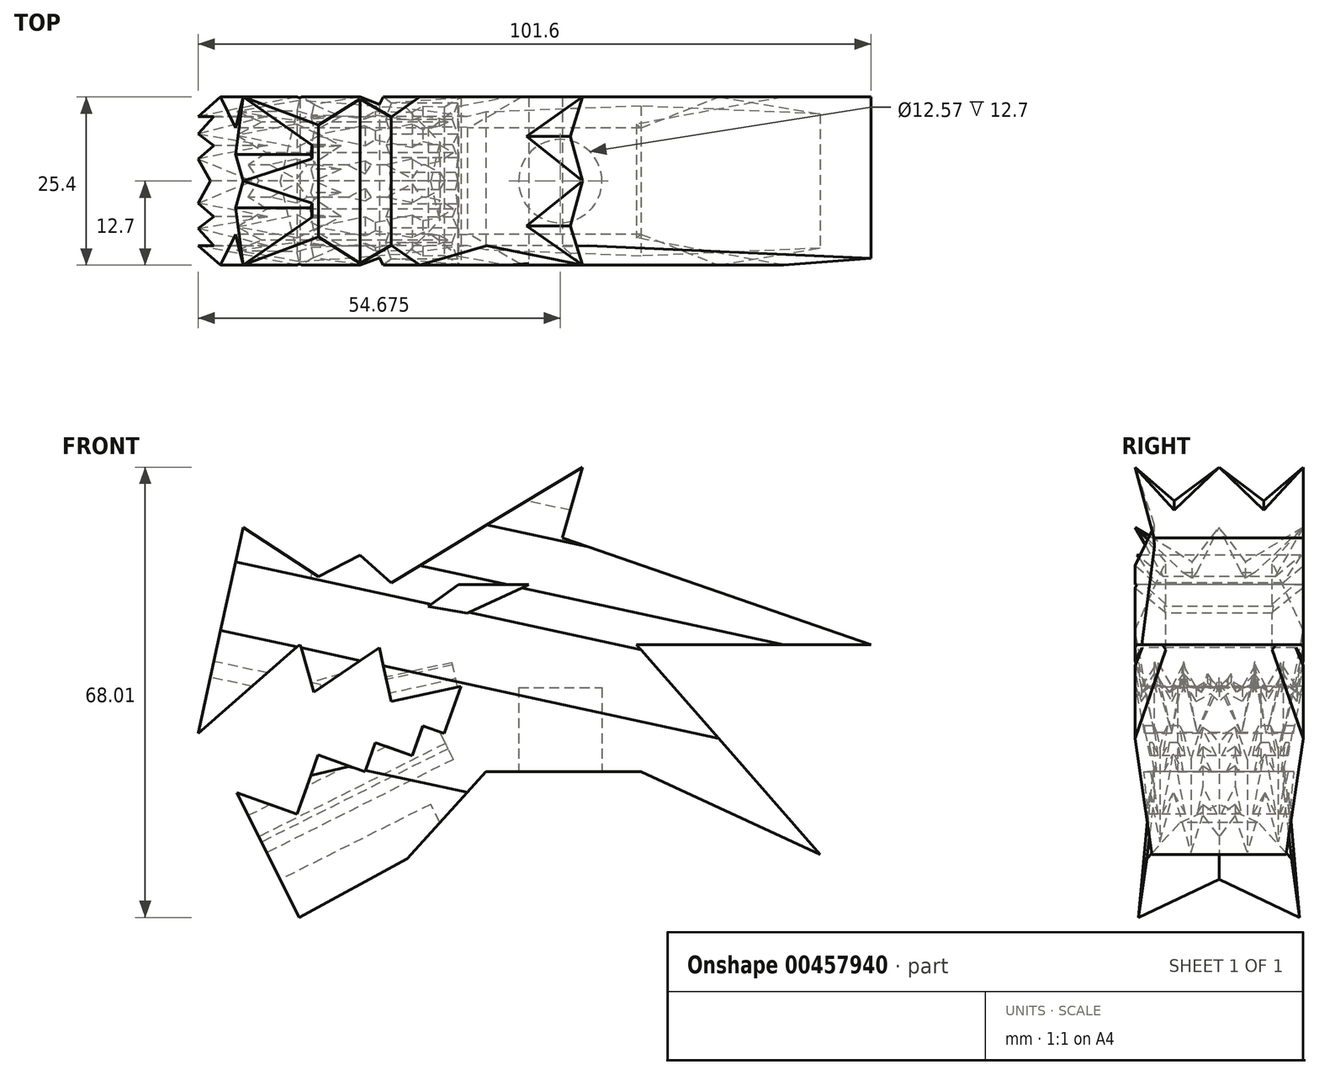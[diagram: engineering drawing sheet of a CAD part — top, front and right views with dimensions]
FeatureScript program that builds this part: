
annotation { "Feature Type Name" : "Feature", "Feature Type Description" : "" }
export const myFeature = defineFeature(function(context is Context, id is Id, definition is map)
    precondition{}
    {
        {
            var Q0;
            Q0=qCreatedBy(makeId("Front.planeOp"),FACE);
            var sketch = newSketch(context, id + "F0", { "sketchPlane" : qUnion([Q0])});
            skLineSegment(sketch, "E0", {"start": v(0, 0) * mm, "end": v(-25.28, -27.85) * mm});
            skLineSegment(sketch, "E1", {"start": v(-25.28, -27.85) * mm, "end": v(-37.63, -3.15) * mm});
            skLineSegment(sketch, "E2", {"start": v(-37.63, -3.15) * mm, "end": v(-28.55, -6.4) * mm});
            skLineSegment(sketch, "E3", {"start": v(-28.55, -6.4) * mm, "end": v(-25.34, 2.53) * mm});
            skLineSegment(sketch, "E4", {"start": v(-25.34, 2.53) * mm, "end": v(-18.28, 0) * mm});
            skLineSegment(sketch, "E5", {"start": v(-18.28, 0) * mm, "end": v(-16.7, 4.4) * mm});
            skLineSegment(sketch, "E6", {"start": v(-16.7, 4.4) * mm, "end": v(-11.16, 2.42) * mm});
            skLineSegment(sketch, "E7", {"start": v(-11.16, 2.42) * mm, "end": v(-9.54, 6.93) * mm});
            skLineSegment(sketch, "E8", {"start": v(-9.54, 6.93) * mm, "end": v(-6.35, 5.78) * mm});
            skLineSegment(sketch, "E9", {"start": v(-6.35, 5.78) * mm, "end": v(-3.79, 12.91) * mm});
            skLineSegment(sketch, "E10", {"start": v(-3.79, 12.91) * mm, "end": v(-14.33, 10.6) * mm});
            skLineSegment(sketch, "E11", {"start": v(-14.33, 10.6) * mm, "end": v(-16.11, 18.75) * mm});
            skLineSegment(sketch, "E12", {"start": v(-16.11, 18.75) * mm, "end": v(-25.98, 12) * mm});
            skLineSegment(sketch, "E13", {"start": v(-25.98, 12) * mm, "end": v(-28.08, 19.22) * mm});
            skLineSegment(sketch, "E14", {"start": v(-28.08, 19.22) * mm, "end": v(-43.46, 5.78) * mm});
            skLineSegment(sketch, "E15", {"start": v(-43.46, 5.78) * mm, "end": v(-36.7, 36.93) * mm});
            skLineSegment(sketch, "E16", {"start": v(-36.7, 36.93) * mm, "end": v(-25.28, 29.48) * mm});
            skLineSegment(sketch, "E17", {"start": v(-25.28, 29.48) * mm, "end": v(-19, 32.74) * mm});
            skLineSegment(sketch, "E18", {"start": v(-19, 32.74) * mm, "end": v(-14.33, 28.55) * mm});
            skLineSegment(sketch, "E19", {"start": v(-14.33, 28.55) * mm, "end": v(14.56, 46.02) * mm});
            skLineSegment(sketch, "E20", {"start": v(14.56, 46.02) * mm, "end": v(11.53, 35.3) * mm});
            skLineSegment(sketch, "E21", {"start": v(11.53, 35.3) * mm, "end": v(58.14, 19.22) * mm});
            skLineSegment(sketch, "E22", {"start": v(58.14, 19.22) * mm, "end": v(22.72, 19.22) * mm});
            skLineSegment(sketch, "E23", {"start": v(22.72, 19.22) * mm, "end": v(50.45, -12.47) * mm});
            skLineSegment(sketch, "E24", {"start": v(50.45, -12.47) * mm, "end": v(23.42, 0) * mm});
            skLineSegment(sketch, "E25", {"start": v(23.42, 0) * mm, "end": v(0, 0) * mm});
            skLineSegment(sketch, "E26", {"start": v(-8.76, 24.95) * mm, "end": v(-4.13, 28.26) * mm});
            skLineSegment(sketch, "E27", {"start": v(-4.13, 28.26) * mm, "end": v(6.44, 28.26) * mm});
            skLineSegment(sketch, "E28", {"start": v(6.44, 28.26) * mm, "end": v(-2.8, 23.96) * mm});
            skLineSegment(sketch, "E29", {"start": v(-2.8, 23.96) * mm, "end": v(-8.76, 24.95) * mm});
            skSolve(sketch);
        }
        {
            var Q0;
            Q0=makeQuery(id+"F0.imprint","IMPRINT",FACE,{"disambiguationData":[TD([[makeQuery(id+"F0.imprint","IMPRINT",EDGE,{"derivedFrom":sQuery(id+"F0.wireOp",EDGE,"E0")}),-1.0]])]});
            extrude(context, id + "F1", {"entities" : qUnion([Q0]), "oppositeDirection" : true, "depth" : 25.4 * mm, "offsetDistance" : 25.4 * mm});
        }
        {
            var Q0;
            Q0=makeQuery(id+"F1.opExtrude","SWEPT_FACE",FACE,{"disambiguationData":[OSD([sQuery(id+"F0.wireOp",EDGE,"E15")])]});
            cPlane(context, id + "F2", {"entities" : qUnion([Q0]), "cplaneType" : CPlaneType.OFFSET, "offset" : 25.4 * mm, "width" : 152.4 * mm, "height" : 152.4 * mm});
        }
        {
            var Q0;
            Q0=qCreatedBy(id+"F2.planeOp",FACE);
            var sketch = newSketch(context, id + "F3", { "sketchPlane" : qUnion([Q0])});
            skPoint(sketch, "E30.0", {"position": v(-25.4, 48.06) * mm});
            skPoint(sketch, "E31.0", {"position": v(0, 48.06) * mm});
            skPoint(sketch, "E32.0", {"position": v(-12.7, 48.06) * mm});
            skPoint(sketch, "E33.0", {"position": v(-12.7, 28.31) * mm});
            skPoint(sketch, "E34.0", {"position": v(-25.4, 28.31) * mm});
            skPoint(sketch, "E35.0", {"position": v(0, 28.31) * mm});
            skPoint(sketch, "E36.0", {"position": v(-25.4, 36.46) * mm});
            skPoint(sketch, "E37.0", {"position": v(0, 36.95) * mm});
            skPoint(sketch, "E38.0", {"position": v(-25.4, 12.38) * mm});
            skPoint(sketch, "E39.0", {"position": v(0, 12.38) * mm});
            skPoint(sketch, "E40.0", {"position": v(-25.4, 0) * mm});
            skPoint(sketch, "E41.0", {"position": v(0, 0) * mm});
            skPoint(sketch, "E42.0", {"position": v(-12.7, -3.56) * mm});
            skLineSegment(sketch, "E43", {"start": v(-25.4, 28.31) * mm, "end": v(-25.4, 48.06) * mm});
            skLineSegment(sketch, "E44", {"start": v(-12.7, 48.06) * mm, "end": v(-19.48, 41.3) * mm});
            skLineSegment(sketch, "E45", {"start": v(-19.48, 41.3) * mm, "end": v(-25.4, 48.06) * mm});
            skLineSegment(sketch, "E46", {"start": v(-25.4, 48.06) * mm, "end": v(-22.44, 36.46) * mm});
            skPoint(sketch, "E46.endSnap0", {"position": v(-22.44, 44.68) * mm});
            skLineSegment(sketch, "E47", {"start": v(-22.44, 36.46) * mm, "end": v(-25.4, 28.31) * mm});
            skLineSegment(sketch, "E48", {"start": v(-25.4, 28.31) * mm, "end": v(-20.73, 22.97) * mm});
            skLineSegment(sketch, "E49", {"start": v(-20.73, 22.97) * mm, "end": v(-25.4, 12.38) * mm});
            skLineSegment(sketch, "E50", {"start": v(-25.4, 12.38) * mm, "end": v(-22.44, -3.65) * mm});
            skLineSegment(sketch, "E51", {"start": v(-22.44, -3.65) * mm, "end": v(-25.4, -32.74) * mm});
            skLineSegment(sketch, "E52", {"start": v(-25.4, -32.74) * mm, "end": v(-12.7, -28.11) * mm});
            skLineSegment(sketch, "E53", {"start": v(-12.7, -28.11) * mm, "end": v(-12.7, -32.74) * mm});
            skLineSegment(sketch, "E54", {"start": v(-12.7, 48.06) * mm, "end": v(-12.7, -32.74) * mm});
            skLineSegment(sketch, "E55.MirrorCS", {"start": v(-12.7, 48.06) * mm, "end": v(-5.92, 41.3) * mm});
            skLineSegment(sketch, "E56.MirrorCS", {"start": v(-5.92, 41.3) * mm, "end": v(0, 48.06) * mm});
            skLineSegment(sketch, "E57.MirrorCS", {"start": v(0, 48.06) * mm, "end": v(-2.96, 36.46) * mm});
            skLineSegment(sketch, "E58.MirrorCS", {"start": v(-2.96, 36.46) * mm, "end": v(0, 28.31) * mm});
            skLineSegment(sketch, "E59.MirrorCS", {"start": v(0, 28.31) * mm, "end": v(-4.67, 22.97) * mm});
            skLineSegment(sketch, "E60.MirrorCS", {"start": v(-2.96, -3.65) * mm, "end": v(0, -32.74) * mm});
            skLineSegment(sketch, "E61.MirrorCS", {"start": v(0, 12.38) * mm, "end": v(-2.96, -3.65) * mm});
            skLineSegment(sketch, "E62.MirrorCS", {"start": v(-4.67, 22.97) * mm, "end": v(0, 12.38) * mm});
            skLineSegment(sketch, "E63.MirrorCS", {"start": v(0, -32.74) * mm, "end": v(-12.7, -28.11) * mm});
            skLineSegment(sketch, "E64", {"start": v(-35.26, 55.46) * mm, "end": v(-35.26, -53.24) * mm});
            skLineSegment(sketch, "E65", {"start": v(-35.26, -53.24) * mm, "end": v(17.4, -53.24) * mm});
            skLineSegment(sketch, "E66", {"start": v(17.4, -53.24) * mm, "end": v(14.5, 59.12) * mm});
            skLineSegment(sketch, "E67", {"start": v(14.5, 59.12) * mm, "end": v(-35.26, 55.46) * mm});
            skSolve(sketch);
        }
        {
            var Q0;
            Q0=makeQuery(id+"F3.imprint","IMPRINT",FACE,{"disambiguationData":[TD([[makeQuery(id+"F3.imprint","IMPRINT",EDGE,{"derivedFrom":sQuery(id+"F3.wireOp",EDGE,"E43")}),1.0]])]});
            extrude(context, id + "F4", {"entities" : qUnion([Q0]), "operationType" : NewBodyOperationType.REMOVE, "oppositeDirection" : true, "depth" : 169.93 * mm, "offsetDistance" : 25.4 * mm});
        }
        {
            var Q0;
            Q0=makeQuery(id+"F1.opExtrude","SWEPT_FACE",FACE,{"disambiguationData":[OSD([sQuery(id+"F0.wireOp",EDGE,"E15")])]});
            var sketch = newSketch(context, id + "F5", { "sketchPlane" : qUnion([Q0])});
            skPoint(sketch, "E68.0", {"position": v(-12.7, 28.31) * mm});
            skLineSegment(sketch, "E69", {"start": v(-12.7, 28.31) * mm, "end": v(-12.7, -3.56) * mm});
            skLineSegment(sketch, "E70", {"start": v(-25.4, 28.31) * mm, "end": v(-16.72, 22.98) * mm});
            skLineSegment(sketch, "E71", {"start": v(-16.72, 22.98) * mm, "end": v(-12.7, 28.31) * mm});
            skLineSegment(sketch, "E72.MirrorCS", {"start": v(-8.68, 22.98) * mm, "end": v(-12.7, 28.31) * mm});
            skLineSegment(sketch, "E73.MirrorCS", {"start": v(0, 28.31) * mm, "end": v(-8.68, 22.98) * mm});
            skLineSegment(sketch, "E74", {"start": v(-22.45, -3.56) * mm, "end": v(-22.45, 7.58) * mm});
            skLineSegment(sketch, "E75", {"start": v(-22.45, 7.58) * mm, "end": v(-19.84, -3.56) * mm});
            skLineSegment(sketch, "E76", {"start": v(-19.84, -3.56) * mm, "end": v(-18.06, 7.58) * mm});
            skLineSegment(sketch, "E77", {"start": v(-18.06, 7.58) * mm, "end": v(-16.05, -3.56) * mm});
            skLineSegment(sketch, "E78", {"start": v(-16.05, -3.56) * mm, "end": v(-12.7, 5.12) * mm});
            skLineSegment(sketch, "E79.MirrorCS", {"start": v(-9.35, -3.56) * mm, "end": v(-12.7, 5.12) * mm});
            skLineSegment(sketch, "E80.MirrorCS", {"start": v(-7.34, 7.58) * mm, "end": v(-9.35, -3.56) * mm});
            skLineSegment(sketch, "E81.MirrorCS", {"start": v(-5.56, -3.56) * mm, "end": v(-7.34, 7.58) * mm});
            skLineSegment(sketch, "E82.MirrorCS", {"start": v(-2.95, 7.58) * mm, "end": v(-5.56, -3.56) * mm});
            skLineSegment(sketch, "E83.MirrorCS", {"start": v(-2.95, -3.56) * mm, "end": v(-2.95, 7.58) * mm});
            skLineSegment(sketch, "E84", {"start": v(-22.45, -3.56) * mm, "end": v(-2.95, -3.56) * mm});
            skSolve(sketch);
        }
        {
            var Q0;
            {var subQ0=sQuery(id+"F5.wireOp",EDGE,"E70");Q0=makeQuery(id+"F5.imprint","IMPRINT",FACE,{"disambiguationData":[TD([[makeQuery(id+"F5.imprint","IMPRINT",EDGE,{"derivedFrom":subQ0}),1.0]])]});}
            var Q1;
            {var subQ0=sQuery(id+"F5.wireOp",EDGE,"E72.MirrorCS");Q1=makeQuery(id+"F5.imprint","IMPRINT",FACE,{"disambiguationData":[TD([[makeQuery(id+"F5.imprint","IMPRINT",EDGE,{"derivedFrom":subQ0}),-1.0]])]});}
            extrude(context, id + "F6", {"entities" : qUnion([Q0, Q1]), "operationType" : NewBodyOperationType.REMOVE, "oppositeDirection" : true, "depth" : 11.68 * mm, "offsetDistance" : 25.4 * mm});
        }
        {
            var Q0;
            Q0 = qSketchRegion(id + "F5", true);
            extrude(context, id + "F7", {"entities" : qUnion([Q0]), "operationType" : NewBodyOperationType.REMOVE, "oppositeDirection" : true, "depth" : 16.5 * mm, "offsetDistance" : 25.4 * mm});
        }
        {
            var Q0;
            Q0=makeQuery(id+"F1.opExtrude","SWEPT_FACE",FACE,{"disambiguationData":[OSD([sQuery(id+"F0.wireOp",EDGE,"E1")])]});
            var sketch = newSketch(context, id + "F8", { "sketchPlane" : qUnion([Q0])});
            skPoint(sketch, "E85.0", {"position": v(-12.7, 14.02) * mm});
            skPoint(sketch, "E86.0", {"position": v(-12.7, -7.87) * mm});
            skLineSegment(sketch, "E87", {"start": v(-12.7, 14.02) * mm, "end": v(-12.7, -7.87) * mm});
            skLineSegment(sketch, "E88", {"start": v(-23.2, 14.02) * mm, "end": v(-21.63, 5.68) * mm});
            skLineSegment(sketch, "E89", {"start": v(-21.63, 5.68) * mm, "end": v(-19.62, 14.02) * mm});
            skLineSegment(sketch, "E90", {"start": v(-19.62, 14.02) * mm, "end": v(-16.94, 3.9) * mm});
            skLineSegment(sketch, "E91", {"start": v(-16.94, 3.9) * mm, "end": v(-15.15, 10.14) * mm});
            skLineSegment(sketch, "E92", {"start": v(-15.15, 10.14) * mm, "end": v(-12.7, 6.57) * mm});
            skLineSegment(sketch, "E93.MirrorCS", {"start": v(-10.25, 10.14) * mm, "end": v(-12.7, 6.57) * mm});
            skLineSegment(sketch, "E94.MirrorCS", {"start": v(-8.46, 3.9) * mm, "end": v(-10.25, 10.14) * mm});
            skLineSegment(sketch, "E95.MirrorCS", {"start": v(-5.78, 14.02) * mm, "end": v(-8.46, 3.9) * mm});
            skLineSegment(sketch, "E96.MirrorCS", {"start": v(-3.77, 5.68) * mm, "end": v(-5.78, 14.02) * mm});
            skLineSegment(sketch, "E97.MirrorCS", {"start": v(-2.2, 14.02) * mm, "end": v(-3.77, 5.68) * mm});
            skSolve(sketch);
        }
        {
            var Q0;
            {var subQ1=sQuery(id+"F8.wireOp",EDGE,"E93.MirrorCS");Q0=makeQuery(id+"F8.imprint","IMPRINT",FACE,{"disambiguationData":[TD([[makeQuery(id+"F8.imprint","IMPRINT",EDGE,{"derivedFrom":subQ1}),-1.0]])]});}
            var Q1;
            {var subQ1=sQuery(id+"F8.wireOp",EDGE,"E90");Q1=makeQuery(id+"F8.imprint","IMPRINT",FACE,{"disambiguationData":[TD([[makeQuery(id+"F8.imprint","IMPRINT",EDGE,{"derivedFrom":subQ1}),1.0]])]});}
            var Q2;
            {var subQ0=sQuery(id+"F8.wireOp",EDGE,"E88");Q2=makeQuery(id+"F8.imprint","IMPRINT",FACE,{"disambiguationData":[TD([[makeQuery(id+"F8.imprint","IMPRINT",EDGE,{"derivedFrom":subQ0}),1.0]])]});}
            var Q3;
            {var subQ0=sQuery(id+"F8.wireOp",EDGE,"E96.MirrorCS");Q3=makeQuery(id+"F8.imprint","IMPRINT",FACE,{"disambiguationData":[TD([[makeQuery(id+"F8.imprint","IMPRINT",EDGE,{"derivedFrom":subQ0}),-1.0]])]});}
            extrude(context, id + "F9", {"entities" : qUnion([Q0, Q1, Q2, Q3]), "operationType" : NewBodyOperationType.REMOVE, "oppositeDirection" : true, "depth" : 31.5 * mm, "offsetDistance" : 25.4 * mm});
        }
        {
            var Q0;
            Q0=makeQuery(id+"F1.opExtrude","SWEPT_FACE",FACE,{"disambiguationData":[OSD([sQuery(id+"F0.wireOp",EDGE,"E11")])]});
            var sketch = newSketch(context, id + "F10", { "sketchPlane" : qUnion([Q0])});
            skPoint(sketch, "E98.0", {"position": v(-12.7, 17.28) * mm});
            skPoint(sketch, "E99.0", {"position": v(-12.7, 13.42) * mm});
            skLineSegment(sketch, "E100", {"start": v(-12.7, 13.42) * mm, "end": v(-12.7, 19.87) * mm});
            skLineSegment(sketch, "E101", {"start": v(-24.47, 13.42) * mm, "end": v(-21.99, 17.2) * mm});
            skLineSegment(sketch, "E102", {"start": v(-21.99, 17.2) * mm, "end": v(-19.8, 13.42) * mm});
            skLineSegment(sketch, "E103", {"start": v(-19.8, 13.42) * mm, "end": v(-18.15, 16.83) * mm});
            skLineSegment(sketch, "E104", {"start": v(-18.15, 16.83) * mm, "end": v(-16.18, 13.42) * mm});
            skLineSegment(sketch, "E105", {"start": v(-16.18, 13.42) * mm, "end": v(-14, 14.7) * mm});
            skLineSegment(sketch, "E106", {"start": v(-14, 14.7) * mm, "end": v(-12.7, 13.42) * mm});
            skLineSegment(sketch, "E107.MirrorCS", {"start": v(-0.93, 13.42) * mm, "end": v(-3.41, 17.2) * mm});
            skLineSegment(sketch, "E108.MirrorCS", {"start": v(-3.41, 17.2) * mm, "end": v(-5.6, 13.42) * mm});
            skLineSegment(sketch, "E109.MirrorCS", {"start": v(-5.6, 13.42) * mm, "end": v(-7.25, 16.83) * mm});
            skLineSegment(sketch, "E110.MirrorCS", {"start": v(-7.25, 16.83) * mm, "end": v(-9.22, 13.42) * mm});
            skLineSegment(sketch, "E111.MirrorCS", {"start": v(-9.22, 13.42) * mm, "end": v(-11.4, 14.7) * mm});
            skLineSegment(sketch, "E112.MirrorCS", {"start": v(-11.4, 14.7) * mm, "end": v(-12.7, 13.42) * mm});
            skLineSegment(sketch, "E113", {"start": v(-24.47, 13.42) * mm, "end": v(-0.93, 13.42) * mm});
            skSolve(sketch);
        }
        {
            var Q0;
            {var subQ0=sQuery(id+"F10.wireOp",EDGE,"E107.MirrorCS");Q0=makeQuery(id+"F10.imprint","IMPRINT",FACE,{"disambiguationData":[TD([[makeQuery(id+"F10.imprint","IMPRINT",EDGE,{"derivedFrom":subQ0}),1.0]])]});}
            var Q1;
            {var subQ0=sQuery(id+"F10.wireOp",EDGE,"E109.MirrorCS");Q1=makeQuery(id+"F10.imprint","IMPRINT",FACE,{"disambiguationData":[TD([[makeQuery(id+"F10.imprint","IMPRINT",EDGE,{"derivedFrom":subQ0}),1.0]])]});}
            var Q2;
            {var subQ0=sQuery(id+"F10.wireOp",EDGE,"E111.MirrorCS");Q2=makeQuery(id+"F10.imprint","IMPRINT",FACE,{"disambiguationData":[TD([[makeQuery(id+"F10.imprint","IMPRINT",EDGE,{"derivedFrom":subQ0}),1.0]])]});}
            var Q3;
            {var subQ0=sQuery(id+"F10.wireOp",EDGE,"E105");Q3=makeQuery(id+"F10.imprint","IMPRINT",FACE,{"disambiguationData":[TD([[makeQuery(id+"F10.imprint","IMPRINT",EDGE,{"derivedFrom":subQ0}),-1.0]])]});}
            var Q4;
            {var subQ0=sQuery(id+"F10.wireOp",EDGE,"E103");Q4=makeQuery(id+"F10.imprint","IMPRINT",FACE,{"disambiguationData":[TD([[makeQuery(id+"F10.imprint","IMPRINT",EDGE,{"derivedFrom":subQ0}),-1.0]])]});}
            var Q5;
            {var subQ0=sQuery(id+"F10.wireOp",EDGE,"E101");Q5=makeQuery(id+"F10.imprint","IMPRINT",FACE,{"disambiguationData":[TD([[makeQuery(id+"F10.imprint","IMPRINT",EDGE,{"derivedFrom":subQ0}),-1.0]])]});}
            extrude(context, id + "F11", {"entities" : qUnion([Q0, Q1, Q2, Q3, Q4, Q5]), "operationType" : NewBodyOperationType.REMOVE, "oppositeDirection" : true, "depth" : 10.26 * mm, "offsetDistance" : 25.4 * mm});
        }
        {
            var Q0;
            Q0=makeQuery(id+"F1.opExtrude","SWEPT_FACE",FACE,{"disambiguationData":[OSD([sQuery(id+"F0.wireOp",EDGE,"E13")])]});
            var sketch = newSketch(context, id + "F12", { "sketchPlane" : qUnion([Q0])});
            skPoint(sketch, "E114.0", {"position": v(-12.7, 18.77) * mm});
            skPoint(sketch, "E115.0", {"position": v(-12.7, 22.24) * mm});
            skLineSegment(sketch, "E116", {"start": v(-12.7, 18.77) * mm, "end": v(-12.7, 22.24) * mm});
            skLineSegment(sketch, "E117", {"start": v(-24.26, 18.77) * mm, "end": v(-22.45, 20.31) * mm});
            skLineSegment(sketch, "E118", {"start": v(-22.45, 20.31) * mm, "end": v(-20.2, 18.77) * mm});
            skLineSegment(sketch, "E119", {"start": v(-20.2, 18.77) * mm, "end": v(-18.06, 20.31) * mm});
            skLineSegment(sketch, "E120", {"start": v(-18.06, 20.31) * mm, "end": v(-15.34, 18.77) * mm});
            skLineSegment(sketch, "E121", {"start": v(-15.34, 18.77) * mm, "end": v(-14.46, 20.31) * mm});
            skLineSegment(sketch, "E122", {"start": v(-14.46, 20.31) * mm, "end": v(-12.7, 18.77) * mm});
            skLineSegment(sketch, "E123", {"start": v(-24.26, 18.77) * mm, "end": v(-12.7, 18.77) * mm});
            skLineSegment(sketch, "E124.MirrorCS", {"start": v(-10.94, 20.31) * mm, "end": v(-12.7, 18.77) * mm});
            skLineSegment(sketch, "E125.MirrorCS", {"start": v(-10.06, 18.77) * mm, "end": v(-10.94, 20.31) * mm});
            skLineSegment(sketch, "E126.MirrorCS", {"start": v(-7.34, 20.31) * mm, "end": v(-10.06, 18.77) * mm});
            skLineSegment(sketch, "E127.MirrorCS", {"start": v(-5.2, 18.77) * mm, "end": v(-7.34, 20.31) * mm});
            skLineSegment(sketch, "E128.MirrorCS", {"start": v(-2.95, 20.31) * mm, "end": v(-5.2, 18.77) * mm});
            skLineSegment(sketch, "E129.MirrorCS", {"start": v(-1.14, 18.77) * mm, "end": v(-2.95, 20.31) * mm});
            skLineSegment(sketch, "E130.MirrorCS", {"start": v(-1.14, 18.77) * mm, "end": v(-12.7, 18.77) * mm});
            skSolve(sketch);
        }
        {
            var Q0;
            {var subQ0=sQuery(id+"F12.wireOp",EDGE,"E118");Q0=makeQuery(id+"F12.imprint","IMPRINT",FACE,{"disambiguationData":[TD([[makeQuery(id+"F12.imprint","IMPRINT",EDGE,{"derivedFrom":subQ0}),-1.0]])]});}
            var Q1;
            {var subQ0=sQuery(id+"F12.wireOp",EDGE,"E117");Q1=makeQuery(id+"F12.imprint","IMPRINT",FACE,{"disambiguationData":[TD([[makeQuery(id+"F12.imprint","IMPRINT",EDGE,{"derivedFrom":subQ0}),-1.0]])]});}
            var Q2;
            {var subQ0=sQuery(id+"F12.wireOp",EDGE,"E119");Q2=makeQuery(id+"F12.imprint","IMPRINT",FACE,{"disambiguationData":[TD([[makeQuery(id+"F12.imprint","IMPRINT",EDGE,{"derivedFrom":subQ0}),-1.0]])]});}
            var Q3;
            {var subQ0=sQuery(id+"F12.wireOp",EDGE,"E120");Q3=makeQuery(id+"F12.imprint","IMPRINT",FACE,{"disambiguationData":[TD([[makeQuery(id+"F12.imprint","IMPRINT",EDGE,{"derivedFrom":subQ0}),-1.0]])]});}
            var Q4;
            {var subQ0=sQuery(id+"F12.wireOp",EDGE,"E121");Q4=makeQuery(id+"F12.imprint","IMPRINT",FACE,{"disambiguationData":[TD([[makeQuery(id+"F12.imprint","IMPRINT",EDGE,{"derivedFrom":subQ0}),-1.0]])]});}
            var Q5;
            {var subQ0=sQuery(id+"F12.wireOp",EDGE,"E124.MirrorCS");Q5=makeQuery(id+"F12.imprint","IMPRINT",FACE,{"disambiguationData":[TD([[makeQuery(id+"F12.imprint","IMPRINT",EDGE,{"derivedFrom":subQ0}),1.0]])]});}
            var Q6;
            {var subQ0=sQuery(id+"F12.wireOp",EDGE,"E126.MirrorCS");Q6=makeQuery(id+"F12.imprint","IMPRINT",FACE,{"disambiguationData":[TD([[makeQuery(id+"F12.imprint","IMPRINT",EDGE,{"derivedFrom":subQ0}),1.0]])]});}
            var Q7;
            {var subQ0=sQuery(id+"F12.wireOp",EDGE,"E128.MirrorCS");Q7=makeQuery(id+"F12.imprint","IMPRINT",FACE,{"disambiguationData":[TD([[makeQuery(id+"F12.imprint","IMPRINT",EDGE,{"derivedFrom":subQ0}),1.0]])]});}
            var Q8;
            {var subQ0=sQuery(id+"F12.wireOp",EDGE,"E129.MirrorCS");Q8=makeQuery(id+"F12.imprint","IMPRINT",FACE,{"disambiguationData":[TD([[makeQuery(id+"F12.imprint","IMPRINT",EDGE,{"derivedFrom":subQ0}),1.0]])]});}
            var Q9;
            {var subQ0=sQuery(id+"F12.wireOp",EDGE,"E127.MirrorCS");Q9=makeQuery(id+"F12.imprint","IMPRINT",FACE,{"disambiguationData":[TD([[makeQuery(id+"F12.imprint","IMPRINT",EDGE,{"derivedFrom":subQ0}),1.0]])]});}
            extrude(context, id + "F13", {"entities" : qUnion([Q0, Q1, Q2, Q3, Q4, Q5, Q6, Q7, Q8, Q9]), "operationType" : NewBodyOperationType.REMOVE, "oppositeDirection" : true, "depth" : 9.65 * mm, "offsetDistance" : 25.4 * mm});
        }
        {
            var Q0;
            Q0=makeQuery(id+"F1.opExtrude","SWEPT_FACE",FACE,{"disambiguationData":[OSD([sQuery(id+"F0.wireOp",EDGE,"E1")])]});
            var sketch = newSketch(context, id + "F14", { "sketchPlane" : qUnion([Q0])});
            skPoint(sketch, "E131.0", {"position": v(-12.7, -7.87) * mm});
            skPoint(sketch, "E132.0", {"position": v(-12.7, 6.57) * mm});
            skLineSegment(sketch, "E133", {"start": v(-12.7, 6.57) * mm, "end": v(-12.7, -7.87) * mm});
            skLineSegment(sketch, "E134", {"start": v(-24.95, -13.6) * mm, "end": v(-12.7, -0.65) * mm});
            skLineSegment(sketch, "E135.MirrorCS", {"start": v(-0.45, -13.6) * mm, "end": v(-12.7, -0.65) * mm});
            skLineSegment(sketch, "E136", {"start": v(-24.86, -7.06) * mm, "end": v(-12.7, -0.65) * mm});
            skLineSegment(sketch, "E137.MirrorCS", {"start": v(-0.54, -7.06) * mm, "end": v(-12.7, -0.65) * mm});
            skSolve(sketch);
        }
        {
            var Q0;
            {var subQ3=sQuery(id+"F14.wireOp",EDGE,"E135.MirrorCS");Q0=makeQuery(id+"F14.imprint","IMPRINT",FACE,{"disambiguationData":[TD([[makeQuery(id+"F14.imprint","IMPRINT",EDGE,{"derivedFrom":subQ3}),1.0]])]});}
            var Q1;
            Q1=makeQuery(id+"F4.boolean.opBoolean","COPY",FACE,{"derivedFrom":makeQuery(id+"F4.opExtrude","SWEPT_FACE",FACE,{"disambiguationData":[OSD([sQuery(id+"F3.wireOp",EDGE,"E63.MirrorCS")])]})});
            var Q2;
            {var subQ3=sQuery(id+"F14.wireOp",EDGE,"E134");Q2=makeQuery(id+"F14.imprint","IMPRINT",FACE,{"disambiguationData":[TD([[makeQuery(id+"F14.imprint","IMPRINT",EDGE,{"derivedFrom":subQ3}),-1.0]])]});}
            var Q3;
            Q3=makeQuery(id+"F4.boolean.opBoolean","COPY",FACE,{"derivedFrom":makeQuery(id+"F4.opExtrude","SWEPT_FACE",FACE,{"disambiguationData":[OSD([sQuery(id+"F3.wireOp",EDGE,"E52")])]})});
            var Q4;
            Q4=makeQuery(id+"F14.imprint","IMPRINT",FACE,{"disambiguationData":[TD([[makeQuery(id+"F14.imprint","IMPRINT",EDGE,{"derivedFrom":sQuery(id+"F14.wireOp",EDGE,"E134")}),1.0]])]});
            var Q5;
            Q5=makeQuery(id+"F14.imprint","IMPRINT",FACE,{"disambiguationData":[TD([[makeQuery(id+"F14.imprint","IMPRINT",EDGE,{"derivedFrom":sQuery(id+"F14.wireOp",EDGE,"E135.MirrorCS")}),-1.0]])]});
            extrude(context, id + "F15", {"entities" : qUnion([Q0, Q1, Q2, Q3, Q4, Q5]), "operationType" : NewBodyOperationType.REMOVE, "oppositeDirection" : true, "depth" : 25.4 * mm, "offsetDistance" : 25.4 * mm});
        }
        {
            var Q0;
            Q0=makeQuery(id+"F1.opExtrude","SWEPT_FACE",FACE,{"disambiguationData":[OSD([sQuery(id+"F0.wireOp",EDGE,"E25")])]});
            var sketch = newSketch(context, id + "F16", { "sketchPlane" : qUnion([Q0])});
            skLineSegment(sketch, "E138", {"start": v(0, -2.29) * mm, "end": v(23.42, -24.03) * mm});
            skLineSegment(sketch, "E139", {"start": v(0, -23.11) * mm, "end": v(23.42, -1.37) * mm});
            skPoint(sketch, "E140", {"position": v(11.22, -12.7) * mm});
            skCircle(sketch, "E141", {"center": v(11.22, -12.7) * mm, "radius": 6.29 * mm});
            skSolve(sketch);
        }
        {
            var Q0;
            Q0 = qSketchRegion(id + "F16", true);
            extrude(context, id + "F17", {"entities" : qUnion([Q0]), "operationType" : NewBodyOperationType.REMOVE, "oppositeDirection" : true, "depth" : 12.7 * mm, "offsetDistance" : 25.4 * mm});
        }
    });
